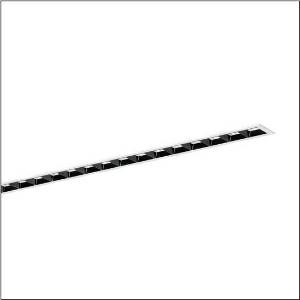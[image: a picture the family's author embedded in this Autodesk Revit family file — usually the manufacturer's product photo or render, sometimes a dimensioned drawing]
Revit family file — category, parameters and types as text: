
# Revit family: silica_21_51mx14tat4w
name_source: partatom
category: Lighting Fixtures
units: mm (PartAtom-declared; Revit-internal decimal feet)

## family parameters
Cut with Voids When Loaded = No
Host = Face
Light Source = No
Part Type = Normal
Room Calculation Point = No
Round Connector Dimension = Use Diameter
Shared = No

## types (1)
- --- (1 x LED, 3280 lm, 32.4 W, 6500K)
    Apparent Load = 32 VA
    CIE Flux Codes = 74 94 99 100 100
    Color Rendering = 80
    Color Temperature = 6500K
    Default Elevation = 1800 mm
    Description = Silica 21, office luminaire, primary light control with darklight reflector, of PMMA, black, light emission: direct distribution, primary light characteristic: asymmetric, installation type: recessed, LED, rated luminous flux: 3.280lm, luminous efficacy: 96lm/W, light colour: 8tw, colour temperature: 2700..6500K, control gear: DALI DT8, with terminal, 3+2-pole, max. 2.5mm², mains connection: 220..240V, AC, 50/60Hz, rated input power: 34.1W, luminaire housing, of aluminium, traffic white (RAL 9016), length: 1.228mm, width: 79mm, height: 53mm, protection rating (complete): IP20, insulation class (complete): insulation class I (protective earthing), certification: CE, ENEC, VDE, permissible operating ambient temperature: 0..+35°C, standard: EN 50419, packaging unit: 1 piece
    Height = 0 mm  [stored 0 ft]
    Lamp = 1 x LED
    Lamp Light Flux = 3280 lm
    Lamp Power = 32.4 W
    Lamp count = 1
    Length = 1227 mm
    Luminous efficacy = 101 lm/W
    Manufacturer = Siteco
    ModVariant = No
    Model = 51MX14TAT4W
    Mounting Place = Ceiling
    Mounting Type = Recessed
    Number of Poles = 1
    OnlyDefault = Yes
    Power Factor = 1
    Product Name = Silica 21
    Product group = office luminaire | ceiling recessed
    ProductGroupID = 400
    Protection Class = Protection class I
    Protection Degree = IP 20
    RLX_Detail_Level = 1
    RLX_Emergency_Light_Flux = 0 lm
    RLX_Emergency_Type = 0
    RLX_Emergency_Type_DB = No
    RlxData = <blob elided: 36117 chars, md5=c2bb2875>
    Socket = socket
    Standby Power = 0 W
    System Light Flux = 3280 lm
    System Power = 32 W
    Type Comments = individual setting
    Type Image = l_1335880.jpg
    URL = http://relux.com
    VarID = @adj_139529
    Voltage = 0 V
    Weight = 0.00 kg
    Width = 79 mm

note: [stored X ft] marks values corroborated as IEEE doubles in the binary element streams (Revit-internal decimal feet)

## geometry (parser evidence)
native form markers: Blend x4, Sweep x10
no freeform markers — native parametric forms only
